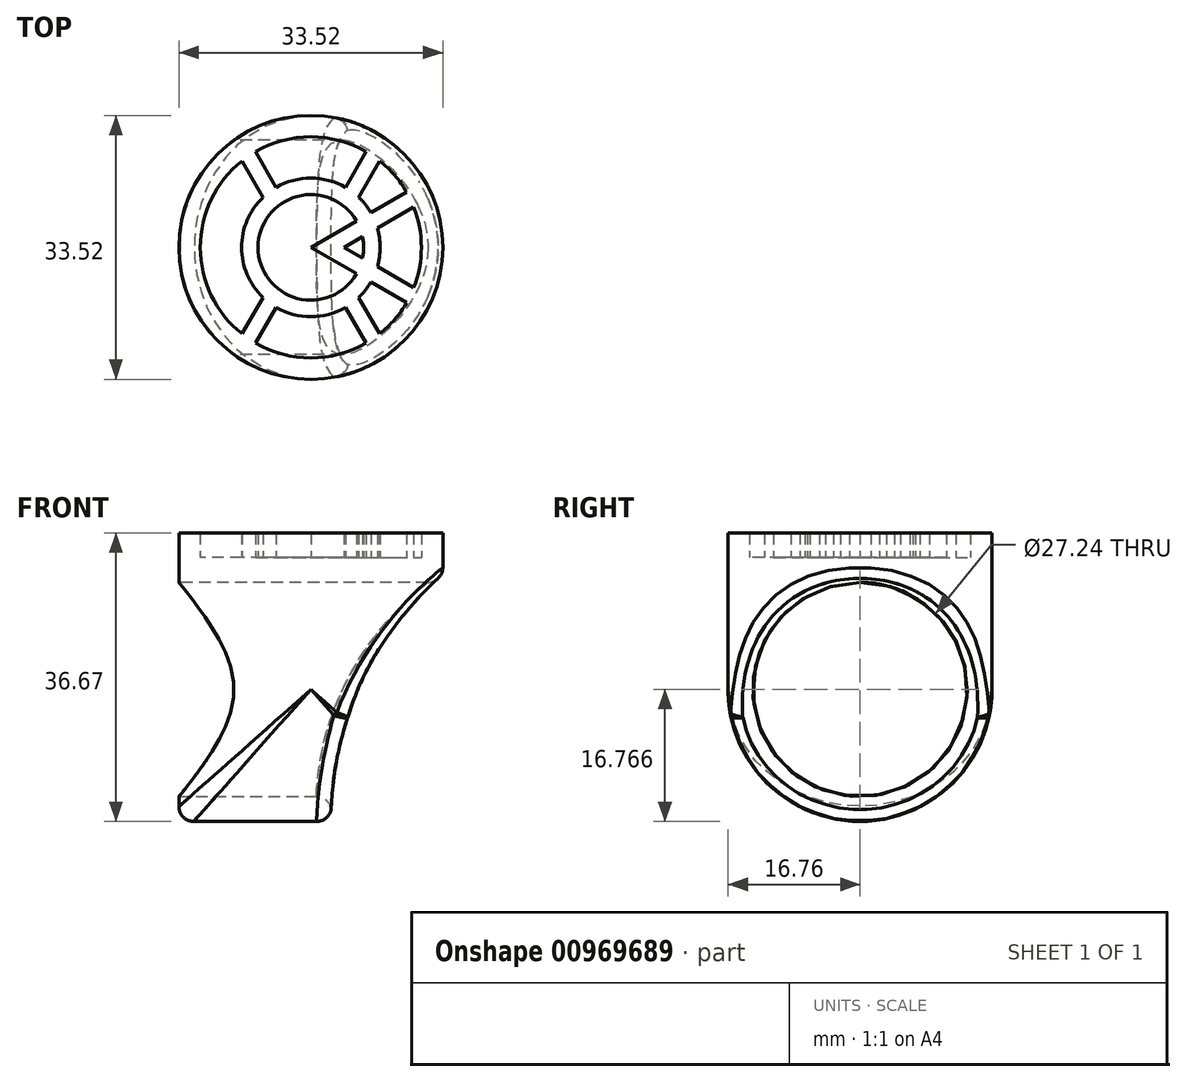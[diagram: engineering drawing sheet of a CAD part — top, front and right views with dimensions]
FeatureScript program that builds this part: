
annotation { "Feature Type Name" : "Feature", "Feature Type Description" : "" }
export const myFeature = defineFeature(function(context is Context, id is Id, definition is map)
    precondition{}
    {
        {
            var Q0;
            Q0=qCreatedBy(makeId("Top.planeOp"),FACE);
            var sketch = newSketch(context, id + "F0", { "sketchPlane" : qUnion([Q0])});
            skCircle(sketch, "E0", {"center": v(0, 0) * mm, "radius": 101.6 * mm});
            skCircle(sketch, "E1.0", {"center": v(0, 0) * mm, "radius": 85.1 * mm});
            skCircle(sketch, "E2.0", {"center": v(0, 0) * mm, "radius": 53.34 * mm});
            skCircle(sketch, "E3.0", {"center": v(0, 0) * mm, "radius": 40.64 * mm});
            skLineSegment(sketch, "E4", {"start": v(0, 0) * mm, "end": v(87.99, 50.8) * mm});
            skLineSegment(sketch, "E5", {"start": v(0, 0) * mm, "end": v(87.99, -50.8) * mm});
            skLineSegment(sketch, "E6.0", {"start": v(25.4, 0) * mm, "end": v(93.65, 39.4) * mm});
            skLineSegment(sketch, "E7.0", {"start": v(25.4, 0) * mm, "end": v(93.65, -39.4) * mm});
            skLineSegment(sketch, "E8", {"start": v(0, 0) * mm, "end": v(50.8, 87.99) * mm});
            skLineSegment(sketch, "E9.0", {"start": v(36.9, 38.52) * mm, "end": v(61.4, 80.95) * mm});
            skLineSegment(sketch, "E10", {"start": v(0, -40.64) * mm, "end": v(0, 0) * mm});
            skLineSegment(sketch, "E11", {"start": v(25.4, 0) * mm, "end": v(0, 0) * mm});
            skLineSegment(sketch, "E12.MirrorCS", {"start": v(36.9, -38.52) * mm, "end": v(61.4, -80.95) * mm});
            skLineSegment(sketch, "E13.MirrorCS", {"start": v(0, 0) * mm, "end": v(50.8, -87.99) * mm});
            skLineSegment(sketch, "E14.MirrorCS", {"start": v(0, 0) * mm, "end": v(-50.8, 87.99) * mm});
            skLineSegment(sketch, "E15.MirrorCS", {"start": v(-36.9, 38.52) * mm, "end": v(-61.4, 80.95) * mm});
            skLineSegment(sketch, "E16.MirrorCS", {"start": v(-36.9, -38.52) * mm, "end": v(-61.4, -80.95) * mm});
            skLineSegment(sketch, "E17.MirrorCS", {"start": v(0, 0) * mm, "end": v(-50.8, -87.99) * mm});
            skSolve(sketch);
        }
        {
            var Q0;
            Q0 = qSketchRegion(id + "F0", true);
            var Q1;
            {var subQ0=sQuery(id+"F0.wireOp",EDGE,"E6.0");var subQ1=sQuery(id+"F0.wireOp",EDGE,"E1.0");var subQ2=makeQuery(id+"F0.imprint","INTERSECT",VERTEX,{"derivedFrom":[subQ1,subQ0]});Q1=makeQuery(id+"F0.imprint","IMPRINT",FACE,{"disambiguationData":[TD([[makeQuery(id+"F0.imprint","IMPRINT",EDGE,{"disambiguationData":[TD([[subQ2,-1.0]])],"derivedFrom":subQ1}),1.0]])]});}
            var Q2;
            {var subQ0=sQuery(id+"F0.wireOp",EDGE,"E9.0");var subQ1=sQuery(id+"F0.wireOp",EDGE,"E1.0");var subQ2=makeQuery(id+"F0.imprint","INTERSECT",VERTEX,{"derivedFrom":[subQ1,subQ0]});Q2=makeQuery(id+"F0.imprint","IMPRINT",FACE,{"disambiguationData":[TD([[makeQuery(id+"F0.imprint","IMPRINT",EDGE,{"disambiguationData":[TD([[subQ2,-1.0]])],"derivedFrom":subQ1}),1.0]])]});}
            var Q3;
            {var subQ1=sQuery(id+"F0.wireOp",EDGE,"E2.0");var subQ7=makeQuery(id+"F0.imprint","INTERSECT",VERTEX,{"derivedFrom":[subQ1,sQuery(id+"F0.wireOp",EDGE,"E9.0")]});Q3=makeQuery(id+"F0.imprint","IMPRINT",FACE,{"disambiguationData":[TD([[makeQuery(id+"F0.imprint","IMPRINT",EDGE,{"disambiguationData":[TD([[subQ7,1.0]])],"derivedFrom":subQ1}),1.0]])]});}
            var Q4;
            {var subQ0=sQuery(id+"F0.wireOp",EDGE,"E8");var subQ1=sQuery(id+"F0.wireOp",EDGE,"E2.0");var subQ2=makeQuery(id+"F0.imprint","INTERSECT",VERTEX,{"derivedFrom":[subQ1,subQ0]});Q4=makeQuery(id+"F0.imprint","IMPRINT",FACE,{"disambiguationData":[TD([[makeQuery(id+"F0.imprint","IMPRINT",EDGE,{"disambiguationData":[TD([[subQ2,-1.0]])],"derivedFrom":subQ1}),1.0]])]});}
            var Q5;
            {var subQ0=sQuery(id+"F0.wireOp",EDGE,"E2.0");var subQ8=makeQuery(id+"F0.imprint","INTERSECT",VERTEX,{"derivedFrom":[subQ0,sQuery(id+"F0.wireOp",EDGE,"E15.MirrorCS")]});Q5=makeQuery(id+"F0.imprint","IMPRINT",FACE,{"disambiguationData":[TD([[makeQuery(id+"F0.imprint","IMPRINT",EDGE,{"disambiguationData":[TD([[subQ8,1.0]])],"derivedFrom":subQ0}),1.0]])]});}
            var Q6;
            {var subQ0=sQuery(id+"F0.wireOp",EDGE,"E14.MirrorCS");var subQ1=sQuery(id+"F0.wireOp",EDGE,"E1.0");var subQ2=makeQuery(id+"F0.imprint","INTERSECT",VERTEX,{"derivedFrom":[subQ1,subQ0]});Q6=makeQuery(id+"F0.imprint","IMPRINT",FACE,{"disambiguationData":[TD([[makeQuery(id+"F0.imprint","IMPRINT",EDGE,{"disambiguationData":[TD([[subQ2,-1.0]])],"derivedFrom":subQ1}),1.0]])]});}
            var Q7;
            {var subQ0=sQuery(id+"F0.wireOp",EDGE,"E16.MirrorCS");var subQ1=sQuery(id+"F0.wireOp",EDGE,"E1.0");var subQ2=makeQuery(id+"F0.imprint","INTERSECT",VERTEX,{"derivedFrom":[subQ1,subQ0]});Q7=makeQuery(id+"F0.imprint","IMPRINT",FACE,{"disambiguationData":[TD([[makeQuery(id+"F0.imprint","IMPRINT",EDGE,{"disambiguationData":[TD([[subQ2,-1.0]])],"derivedFrom":subQ1}),1.0]])]});}
            var Q8;
            {var subQ0=sQuery(id+"F0.wireOp",EDGE,"E13.MirrorCS");var subQ1=sQuery(id+"F0.wireOp",EDGE,"E2.0");var subQ2=makeQuery(id+"F0.imprint","INTERSECT",VERTEX,{"derivedFrom":[subQ1,subQ0]});Q8=makeQuery(id+"F0.imprint","IMPRINT",FACE,{"disambiguationData":[TD([[makeQuery(id+"F0.imprint","IMPRINT",EDGE,{"disambiguationData":[TD([[subQ2,1.0]])],"derivedFrom":subQ1}),1.0]])]});}
            var Q9;
            {var subQ0=sQuery(id+"F0.wireOp",EDGE,"E12.MirrorCS");var subQ1=sQuery(id+"F0.wireOp",EDGE,"E1.0");var subQ2=makeQuery(id+"F0.imprint","INTERSECT",VERTEX,{"derivedFrom":[subQ1,subQ0]});Q9=makeQuery(id+"F0.imprint","IMPRINT",FACE,{"disambiguationData":[TD([[makeQuery(id+"F0.imprint","IMPRINT",EDGE,{"disambiguationData":[TD([[subQ2,1.0]])],"derivedFrom":subQ1}),1.0]])]});}
            var Q10;
            {var subQ5=sQuery(id+"F0.wireOp",EDGE,"E2.0");var subQ8=makeQuery(id+"F0.imprint","INTERSECT",VERTEX,{"derivedFrom":[subQ5,sQuery(id+"F0.wireOp",EDGE,"E12.MirrorCS")]});Q10=makeQuery(id+"F0.imprint","IMPRINT",FACE,{"disambiguationData":[TD([[makeQuery(id+"F0.imprint","IMPRINT",EDGE,{"disambiguationData":[TD([[subQ8,1.0]])],"derivedFrom":subQ5}),1.0]])]});}
            var Q11;
            {var subQ0=sQuery(id+"F0.wireOp",EDGE,"E5");var subQ1=sQuery(id+"F0.wireOp",EDGE,"E1.0");var subQ2=makeQuery(id+"F0.imprint","INTERSECT",VERTEX,{"derivedFrom":[subQ1,subQ0]});Q11=makeQuery(id+"F0.imprint","IMPRINT",FACE,{"disambiguationData":[TD([[makeQuery(id+"F0.imprint","IMPRINT",EDGE,{"disambiguationData":[TD([[subQ2,-1.0]])],"derivedFrom":subQ1}),1.0]])]});}
            var Q12;
            {var subQ0=sQuery(id+"F0.wireOp",EDGE,"E5");var subQ1=sQuery(id+"F0.wireOp",EDGE,"E2.0");var subQ2=makeQuery(id+"F0.imprint","INTERSECT",VERTEX,{"derivedFrom":[subQ1,subQ0]});Q12=makeQuery(id+"F0.imprint","IMPRINT",FACE,{"disambiguationData":[TD([[makeQuery(id+"F0.imprint","IMPRINT",EDGE,{"disambiguationData":[TD([[subQ2,-1.0]])],"derivedFrom":subQ1}),1.0]])]});}
            var Q13;
            {var subQ0=sQuery(id+"F0.wireOp",EDGE,"E7.0");var subQ1=sQuery(id+"F0.wireOp",EDGE,"E2.0");var subQ2=makeQuery(id+"F0.imprint","INTERSECT",VERTEX,{"derivedFrom":[subQ1,subQ0]});Q13=makeQuery(id+"F0.imprint","IMPRINT",FACE,{"disambiguationData":[TD([[makeQuery(id+"F0.imprint","IMPRINT",EDGE,{"disambiguationData":[TD([[subQ2,-1.0]])],"derivedFrom":subQ1}),1.0]])]});}
            var Q14;
            {var subQ0=sQuery(id+"F0.wireOp",EDGE,"E6.0");var subQ1=sQuery(id+"F0.wireOp",EDGE,"E2.0");var subQ2=makeQuery(id+"F0.imprint","INTERSECT",VERTEX,{"derivedFrom":[subQ1,subQ0]});Q14=makeQuery(id+"F0.imprint","IMPRINT",FACE,{"disambiguationData":[TD([[makeQuery(id+"F0.imprint","IMPRINT",EDGE,{"disambiguationData":[TD([[subQ2,-1.0]])],"derivedFrom":subQ1}),1.0]])]});}
            var Q15;
            {var subQ5=sQuery(id+"F0.wireOp",EDGE,"E11");Q15=makeQuery(id+"F0.imprint","IMPRINT",FACE,{"disambiguationData":[TD([[makeQuery(id+"F0.imprint","IMPRINT",EDGE,{"derivedFrom":subQ5}),-1.0]])]});}
            var Q16;
            {var subQ5=sQuery(id+"F0.wireOp",EDGE,"E11");Q16=makeQuery(id+"F0.imprint","IMPRINT",FACE,{"disambiguationData":[TD([[makeQuery(id+"F0.imprint","IMPRINT",EDGE,{"derivedFrom":subQ5}),1.0]])]});}
            extrude(context, id + "F1", {"entities" : qUnion([Q0, Q1, Q2, Q3, Q4, Q5, Q6, Q7, Q8, Q9, Q10, Q11, Q12, Q13, Q14, Q15, Q16]), "depth" : 19.05 * mm, "offsetDistance" : 25.4 * mm});
        }
        {
            var Q0;
            Q0=makeQuery(id+"F1.opExtrude","CAP_FACE",FACE,{"disambiguationData":[OSD([sQuery(id+"F0.wireOp",EDGE,"E0"),sQuery(id+"F0.wireOp",EDGE,"E1.0"),sQuery(id+"F0.wireOp",EDGE,"E2.0"),sQuery(id+"F0.wireOp",EDGE,"E3.0"),sQuery(id+"F0.wireOp",EDGE,"E4"),sQuery(id+"F0.wireOp",EDGE,"E5"),sQuery(id+"F0.wireOp",EDGE,"E6.0"),sQuery(id+"F0.wireOp",EDGE,"E7.0"),sQuery(id+"F0.wireOp",EDGE,"E8"),sQuery(id+"F0.wireOp",EDGE,"E9.0"),sQuery(id+"F0.wireOp",EDGE,"E12.MirrorCS"),sQuery(id+"F0.wireOp",EDGE,"E13.MirrorCS"),sQuery(id+"F0.wireOp",EDGE,"E14.MirrorCS"),sQuery(id+"F0.wireOp",EDGE,"E15.MirrorCS"),sQuery(id+"F0.wireOp",EDGE,"E16.MirrorCS"),sQuery(id+"F0.wireOp",EDGE,"E17.MirrorCS")])],"isStart":true});
            var sketch = newSketch(context, id + "F2", { "sketchPlane" : qUnion([Q0])});
            skCircle(sketch, "E18", {"center": v(0, 0) * mm, "radius": 101.6 * mm});
            skSolve(sketch);
        }
        {
            var Q0;
            Q0 = qSketchRegion(id + "F2", true);
            extrude(context, id + "F3", {"entities" : qUnion([Q0]), "operationType" : NewBodyOperationType.ADD, "depth" : 6.35 * mm, "offsetDistance" : 25.4 * mm});
        }
        {
            var Q0;
            Q0=qCreatedBy(makeId("Right.planeOp"),FACE);
            var sketch = newSketch(context, id + "F4", { "sketchPlane" : qUnion([Q0])});
            skCircle(sketch, "E19", {"center": v(0, -101.6) * mm, "radius": 82.55 * mm});
            skCircle(sketch, "E20", {"center": v(0, -101.6) * mm, "radius": 101.6 * mm});
            skLineSegment(sketch, "E21", {"start": v(0, 0) * mm, "end": v(0, -56.34) * mm});
            skLineSegment(sketch, "E22", {"start": v(-101.6, -101.6) * mm, "end": v(-101.6, 0) * mm});
            skLineSegment(sketch, "E23", {"start": v(101.6, -101.6) * mm, "end": v(101.6, 0) * mm});
            skLineSegment(sketch, "E24", {"start": v(-101.6, 0) * mm, "end": v(101.6, 0) * mm});
            skSolve(sketch);
        }
        {
            var Q0;
            Q0=makeQuery(id+"F4.imprint","IMPRINT",FACE,{"disambiguationData":[TD([[makeQuery(id+"F4.imprint","IMPRINT",EDGE,{"derivedFrom":sQuery(id+"F4.wireOp",EDGE,"E19")}),-1.0]])]});
            var Q1;
            {var subQ3=sQuery(id+"F4.wireOp",EDGE,"E22");Q1=makeQuery(id+"F4.imprint","IMPRINT",FACE,{"disambiguationData":[TD([[makeQuery(id+"F4.imprint","IMPRINT",EDGE,{"derivedFrom":subQ3}),-1.0]])]});}
            var Q2;
            {var subQ3=sQuery(id+"F4.wireOp",EDGE,"E23");Q2=makeQuery(id+"F4.imprint","IMPRINT",FACE,{"disambiguationData":[TD([[makeQuery(id+"F4.imprint","IMPRINT",EDGE,{"derivedFrom":subQ3}),1.0]])]});}
            extrude(context, id + "F5", {"entities" : qUnion([Q0, Q1, Q2]), "operationType" : NewBodyOperationType.ADD, "depth" : 101.6 * mm, "offsetDistance" : 25.4 * mm, "hasSecondDirection" : true, "secondDirectionOppositeDirection" : true, "secondDirectionDepth" : 101.6 * mm});
        }
        {
            var Q0;
            {var subQ0=sQuery(id+"F4.wireOp",EDGE,"E22");var subQ1=sQuery(id+"F4.wireOp",EDGE,"E24");var subQ2=makeQuery(id+"F5.opExtrude","SWEPT_FACE",FACE,{"disambiguationData":[OSD([subQ1])]});Q0=makeQuery(id+"F5.boolean.opBoolean","SPLIT",FACE,{"disambiguationData":[TD([makeQuery(id+"F1.opExtrude","SWEPT_FACE",FACE,{"disambiguationData":[OSD([sQuery(id+"F0.wireOp",EDGE,"E0")])]}),makeQuery(id+"F3.opExtrude","SWEPT_FACE",FACE,{"disambiguationData":[OSD([sQuery(id+"F2.wireOp",EDGE,"E18")])]}),makeQuery(id+"F5.opExtrude","CAP_FACE",FACE,{"disambiguationData":[OSD([sQuery(id+"F4.wireOp",EDGE,"E19"),sQuery(id+"F4.wireOp",EDGE,"E20"),subQ0,sQuery(id+"F4.wireOp",EDGE,"E23"),subQ1])],"isStart":true}),makeQuery(id+"F5.opExtrude","SWEPT_FACE",FACE,{"disambiguationData":[OSD([subQ0])]}),subQ2])],"derivedFrom":subQ2});}
            var sketch = newSketch(context, id + "F6", { "sketchPlane" : qUnion([Q0])});
            skCircle(sketch, "E25", {"center": v(0, 0) * mm, "radius": 101.6 * mm});
            skLineSegment(sketch, "E26.bottom", {"start": v(-101.6, 101.6) * mm, "end": v(101.6, 101.6) * mm});
            skLineSegment(sketch, "E26.top", {"start": v(-101.6, -101.6) * mm, "end": v(101.6, -101.6) * mm});
            skLineSegment(sketch, "E26.left", {"start": v(-101.6, 101.6) * mm, "end": v(-101.6, -101.6) * mm});
            skLineSegment(sketch, "E26.right", {"start": v(101.6, 101.6) * mm, "end": v(101.6, -101.6) * mm});
            skSolve(sketch);
        }
        {
            var Q0;
            {var subQ0=sQuery(id+"F6.wireOp",EDGE,"E26.left");var subQ1=sQuery(id+"F6.wireOp",EDGE,"E25");var subQ2=makeQuery(id+"F6.imprint","INTERSECT",VERTEX,{"derivedFrom":[subQ1,subQ0]});Q0=makeQuery(id+"F6.imprint","IMPRINT",FACE,{"disambiguationData":[TD([[makeQuery(id+"F6.imprint","IMPRINT",EDGE,{"disambiguationData":[TD([[subQ2,-1.0]])],"derivedFrom":subQ1}),-1.0]])]});}
            var Q1;
            {var subQ0=sQuery(id+"F6.wireOp",EDGE,"E26.top");var subQ1=sQuery(id+"F6.wireOp",EDGE,"E25");var subQ2=makeQuery(id+"F6.imprint","INTERSECT",VERTEX,{"derivedFrom":[subQ1,subQ0]});Q1=makeQuery(id+"F6.imprint","IMPRINT",FACE,{"disambiguationData":[TD([[makeQuery(id+"F6.imprint","IMPRINT",EDGE,{"disambiguationData":[TD([[subQ2,-1.0]])],"derivedFrom":subQ1}),-1.0]])]});}
            var Q2;
            {var subQ0=sQuery(id+"F6.wireOp",EDGE,"E26.bottom");var subQ1=sQuery(id+"F6.wireOp",EDGE,"E25");var subQ2=makeQuery(id+"F6.imprint","INTERSECT",VERTEX,{"derivedFrom":[subQ1,subQ0]});Q2=makeQuery(id+"F6.imprint","IMPRINT",FACE,{"disambiguationData":[TD([[makeQuery(id+"F6.imprint","IMPRINT",EDGE,{"disambiguationData":[TD([[subQ2,1.0]])],"derivedFrom":subQ1}),-1.0]])]});}
            var Q3;
            {var subQ0=sQuery(id+"F6.wireOp",EDGE,"E26.left");var subQ1=sQuery(id+"F6.wireOp",EDGE,"E25");var subQ2=makeQuery(id+"F6.imprint","INTERSECT",VERTEX,{"derivedFrom":[subQ1,subQ0]});Q3=makeQuery(id+"F6.imprint","IMPRINT",FACE,{"disambiguationData":[TD([[makeQuery(id+"F6.imprint","IMPRINT",EDGE,{"disambiguationData":[TD([[subQ2,1.0]])],"derivedFrom":subQ1}),-1.0]])]});}
            extrude(context, id + "F7", {"entities" : qUnion([Q0, Q1, Q2, Q3]), "operationType" : NewBodyOperationType.REMOVE, "endBound" : BoundingType.THROUGH_ALL, "oppositeDirection" : true, "depth" : 25.4 * mm, "offsetDistance" : 25.4 * mm});
        }
        {
            var Q0;
            Q0=qCreatedBy(makeId("Front.planeOp"),FACE);
            var sketch = newSketch(context, id + "F8", { "sketchPlane" : qUnion([Q0])});
            skLineSegment(sketch, "E27", {"start": v(-159.12, -203.2) * mm, "end": v(149.45, -203.2) * mm});
            skLineSegment(sketch, "E28", {"start": v(-101.6, -12.7) * mm, "end": v(42.64, -12.7) * mm});
            skArc(sketch, "E29", {"start": v(-101.6, -12.7) * mm, "mid": v(-38.1, -98.7) * mm, "end": v(-15.6, -203.2) * mm});
            skLineSegment(sketch, "E30", {"start": v(-101.6, -12.7) * mm, "end": v(-101.6, -203.2) * mm});
            skLineSegment(sketch, "E31", {"start": v(-101.6, -203.2) * mm, "end": v(-15.6, -203.2) * mm});
            skLineSegment(sketch, "E32", {"start": v(0, 0) * mm, "end": v(0, -73.39) * mm});
            skLineSegment(sketch, "E33.MirrorCS", {"start": v(101.6, -12.7) * mm, "end": v(101.6, -203.2) * mm});
            skArc(sketch, "E34.MirrorCS", {"start": v(101.6, -12.7) * mm, "mid": v(38.1, -98.7) * mm, "end": v(15.6, -203.2) * mm});
            skLineSegment(sketch, "E35.MirrorCS", {"start": v(101.6, -203.2) * mm, "end": v(15.6, -203.2) * mm});
            skSolve(sketch);
        }
        {
            var Q0;
            {var subQ2=sQuery(id+"F8.wireOp",EDGE,"E33.MirrorCS");var subQ3=sQuery(id+"F8.wireOp",EDGE,"E29");Q0=qUnion([makeQuery(id+"F8.imprint","IMPRINT",FACE,{"disambiguationData":[TD([[makeQuery(id+"F8.imprint","IMPRINT",EDGE,{"derivedFrom":subQ3}),-1.0]])]}),makeQuery(id+"F8.imprint","IMPRINT",FACE,{"disambiguationData":[TD([[makeQuery(id+"F8.imprint","IMPRINT",EDGE,{"derivedFrom":subQ2}),-1.0]])]})]);}
            extrude(context, id + "F9", {"entities" : qUnion([Q0]), "operationType" : NewBodyOperationType.REMOVE, "endBound" : BoundingType.THROUGH_ALL, "oppositeDirection" : true, "depth" : 25.4 * mm, "offsetDistance" : 25.4 * mm, "hasSecondDirection" : true, "secondDirectionBound" : SecondDirectionBoundingType.THROUGH_ALL, "secondDirectionOppositeDirection" : false, "secondDirectionDepth" : 25.4 * mm});
        }
        {
            var Q0;
            Q0=makeQuery(id+"F9.boolean.opBoolean","COPY",FACE,{"derivedFrom":makeQuery(id+"F9.opExtrude","SWEPT_FACE",FACE,{"disambiguationData":[OSD([sQuery(id+"F8.wireOp",EDGE,"E29")])]})});
            var Q1;
            Q1=makeQuery(id+"F9.boolean.opBoolean","COPY",FACE,{"derivedFrom":makeQuery(id+"F9.opExtrude","SWEPT_FACE",FACE,{"disambiguationData":[OSD([sQuery(id+"F8.wireOp",EDGE,"E34.MirrorCS")])]})});
            var Q2;
            {var subQ0=sQuery(id+"F6.wireOp",EDGE,"E25");Q2=makeQuery(id+"F9.boolean.opBoolean","SPLIT",EDGE,{"disambiguationData":[OD(0.0)],"derivedFrom":makeQuery(id+"F7.boolean.opBoolean","INTERSECT",EDGE,{"derivedFrom":[makeQuery(id+"F5.opExtrude","SWEPT_FACE",FACE,{"disambiguationData":[OSD([sQuery(id+"F4.wireOp",EDGE,"E20")])]}),makeQuery(id+"F7.opExtrude","SWEPT_FACE",FACE,{"disambiguationData":[OSD([subQ0]),TDD([makeQuery(id+"F6.imprint","IMPRINT",EDGE,{"disambiguationData":[TD([[makeQuery(id+"F6.imprint","INTERSECT",VERTEX,{"derivedFrom":[subQ0,sQuery(id+"F6.wireOp",EDGE,"E26.bottom")]}),1.0]])],"derivedFrom":subQ0})])]}),makeQuery(id+"F7.opExtrude","SWEPT_FACE",FACE,{"disambiguationData":[OSD([subQ0]),TDD([makeQuery(id+"F6.imprint","IMPRINT",EDGE,{"disambiguationData":[TD([[makeQuery(id+"F6.imprint","INTERSECT",VERTEX,{"derivedFrom":[subQ0,sQuery(id+"F6.wireOp",EDGE,"E26.top")]}),-1.0]])],"derivedFrom":subQ0})])]})]})});}
            var Q3;
            {var subQ0=sQuery(id+"F6.wireOp",EDGE,"E25");var subQ1=makeQuery(id+"F6.imprint","INTERSECT",VERTEX,{"derivedFrom":[subQ0,sQuery(id+"F6.wireOp",EDGE,"E26.left")]});Q3=makeQuery(id+"F9.boolean.opBoolean","SPLIT",EDGE,{"disambiguationData":[OD(0.0)],"derivedFrom":makeQuery(id+"F7.boolean.opBoolean","INTERSECT",EDGE,{"derivedFrom":[makeQuery(id+"F5.opExtrude","SWEPT_FACE",FACE,{"disambiguationData":[OSD([sQuery(id+"F4.wireOp",EDGE,"E20")])]}),makeQuery(id+"F7.opExtrude","SWEPT_FACE",FACE,{"disambiguationData":[OSD([subQ0]),TDD([makeQuery(id+"F6.imprint","IMPRINT",EDGE,{"disambiguationData":[TD([[subQ1,1.0]])],"derivedFrom":subQ0})])]}),makeQuery(id+"F7.opExtrude","SWEPT_FACE",FACE,{"disambiguationData":[OSD([subQ0]),TDD([makeQuery(id+"F6.imprint","IMPRINT",EDGE,{"disambiguationData":[TD([[subQ1,-1.0]])],"derivedFrom":subQ0})])]})]})});}
            var Q4;
            {var subQ0=sQuery(id+"F6.wireOp",EDGE,"E25");var subQ1=makeQuery(id+"F6.imprint","INTERSECT",VERTEX,{"derivedFrom":[subQ0,sQuery(id+"F6.wireOp",EDGE,"E26.left")]});Q4=makeQuery(id+"F9.boolean.opBoolean","SPLIT",EDGE,{"disambiguationData":[OD(1.0)],"derivedFrom":makeQuery(id+"F7.boolean.opBoolean","INTERSECT",EDGE,{"derivedFrom":[makeQuery(id+"F5.opExtrude","SWEPT_FACE",FACE,{"disambiguationData":[OSD([sQuery(id+"F4.wireOp",EDGE,"E20")])]}),makeQuery(id+"F7.opExtrude","SWEPT_FACE",FACE,{"disambiguationData":[OSD([subQ0]),TDD([makeQuery(id+"F6.imprint","IMPRINT",EDGE,{"disambiguationData":[TD([[subQ1,1.0]])],"derivedFrom":subQ0})])]}),makeQuery(id+"F7.opExtrude","SWEPT_FACE",FACE,{"disambiguationData":[OSD([subQ0]),TDD([makeQuery(id+"F6.imprint","IMPRINT",EDGE,{"disambiguationData":[TD([[subQ1,-1.0]])],"derivedFrom":subQ0})])]})]})});}
            var Q5;
            {var subQ0=sQuery(id+"F6.wireOp",EDGE,"E25");Q5=makeQuery(id+"F9.boolean.opBoolean","SPLIT",EDGE,{"disambiguationData":[OD(1.0)],"derivedFrom":makeQuery(id+"F7.boolean.opBoolean","INTERSECT",EDGE,{"derivedFrom":[makeQuery(id+"F5.opExtrude","SWEPT_FACE",FACE,{"disambiguationData":[OSD([sQuery(id+"F4.wireOp",EDGE,"E20")])]}),makeQuery(id+"F7.opExtrude","SWEPT_FACE",FACE,{"disambiguationData":[OSD([subQ0]),TDD([makeQuery(id+"F6.imprint","IMPRINT",EDGE,{"disambiguationData":[TD([[makeQuery(id+"F6.imprint","INTERSECT",VERTEX,{"derivedFrom":[subQ0,sQuery(id+"F6.wireOp",EDGE,"E26.bottom")]}),1.0]])],"derivedFrom":subQ0})])]}),makeQuery(id+"F7.opExtrude","SWEPT_FACE",FACE,{"disambiguationData":[OSD([subQ0]),TDD([makeQuery(id+"F6.imprint","IMPRINT",EDGE,{"disambiguationData":[TD([[makeQuery(id+"F6.imprint","INTERSECT",VERTEX,{"derivedFrom":[subQ0,sQuery(id+"F6.wireOp",EDGE,"E26.top")]}),-1.0]])],"derivedFrom":subQ0})])]})]})});}
            fillet(context, id + "F10", {"entities" : qUnion([Q0, Q1, Q2, Q3, Q4, Q5]), "radius" : 11.43 * mm, "tangentPropagation" : true, "allowEdgeOverflow" : false});
        }
        {
            var Q0;
            Q0=makeQuery(id+"F1.opExtrude","SWEPT_BODY",BODY,{"disambiguationData":[OSD([sQuery(id+"F0.wireOp",EDGE,"E0"),sQuery(id+"F0.wireOp",EDGE,"E1.0"),sQuery(id+"F0.wireOp",EDGE,"E2.0"),sQuery(id+"F0.wireOp",EDGE,"E3.0"),sQuery(id+"F0.wireOp",EDGE,"E4"),sQuery(id+"F0.wireOp",EDGE,"E5"),sQuery(id+"F0.wireOp",EDGE,"E6.0"),sQuery(id+"F0.wireOp",EDGE,"E7.0"),sQuery(id+"F0.wireOp",EDGE,"E8"),sQuery(id+"F0.wireOp",EDGE,"E9.0"),sQuery(id+"F0.wireOp",EDGE,"E12.MirrorCS"),sQuery(id+"F0.wireOp",EDGE,"E13.MirrorCS"),sQuery(id+"F0.wireOp",EDGE,"E14.MirrorCS"),sQuery(id+"F0.wireOp",EDGE,"E15.MirrorCS"),sQuery(id+"F0.wireOp",EDGE,"E16.MirrorCS"),sQuery(id+"F0.wireOp",EDGE,"E17.MirrorCS")])]});
            var Q1;
            Q1=qCreatedBy(makeId("Origin.pointOp"),VERTEX);
            transform(context, id + "F11", {"entities" : qUnion([Q0]), "transformType" : TransformType.SCALE_UNIFORMLY, "scale" : 0.33, "scalePoint" : qUnion([Q1]), "makeCopy" : false});
        }
        {
            var Q0;
            Q0=makeQuery(id+"F1.opExtrude","SWEPT_BODY",BODY,{"disambiguationData":[OSD([sQuery(id+"F0.wireOp",EDGE,"E0"),sQuery(id+"F0.wireOp",EDGE,"E1.0"),sQuery(id+"F0.wireOp",EDGE,"E2.0"),sQuery(id+"F0.wireOp",EDGE,"E3.0"),sQuery(id+"F0.wireOp",EDGE,"E4"),sQuery(id+"F0.wireOp",EDGE,"E5"),sQuery(id+"F0.wireOp",EDGE,"E6.0"),sQuery(id+"F0.wireOp",EDGE,"E7.0"),sQuery(id+"F0.wireOp",EDGE,"E8"),sQuery(id+"F0.wireOp",EDGE,"E9.0"),sQuery(id+"F0.wireOp",EDGE,"E12.MirrorCS"),sQuery(id+"F0.wireOp",EDGE,"E13.MirrorCS"),sQuery(id+"F0.wireOp",EDGE,"E14.MirrorCS"),sQuery(id+"F0.wireOp",EDGE,"E15.MirrorCS"),sQuery(id+"F0.wireOp",EDGE,"E16.MirrorCS"),sQuery(id+"F0.wireOp",EDGE,"E17.MirrorCS")])]});
            var Q1;
            Q1=qCreatedBy(makeId("Origin.pointOp"),VERTEX);
            transform(context, id + "F12", {"entities" : qUnion([Q0]), "transformType" : TransformType.SCALE_UNIFORMLY, "scale" : 0.5, "scalePoint" : qUnion([Q1]), "makeCopy" : false});
        }
    });
